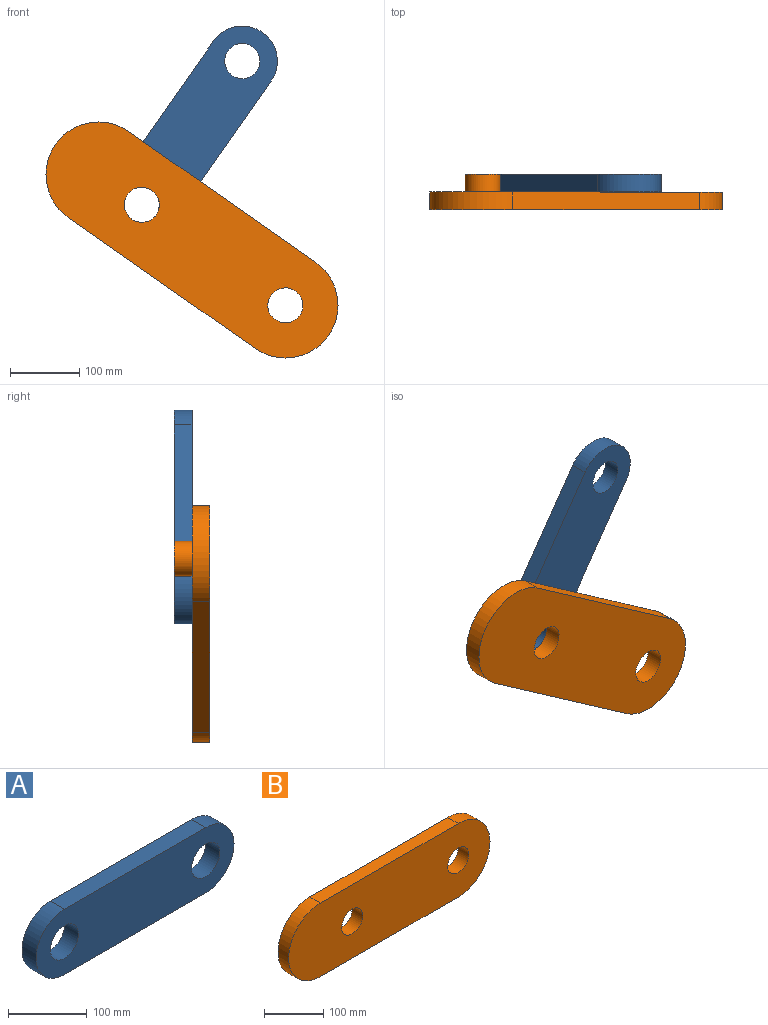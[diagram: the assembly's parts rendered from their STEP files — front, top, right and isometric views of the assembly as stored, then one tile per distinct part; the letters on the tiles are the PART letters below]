
ASSEMBLY  parts=2 mates=1
PART A: 8 faces, bbox 355.6x25.4x101.6 mm
  f0: plane 254x25.4mm, normal (0,0,1), area 6451.6mm2, adj f1,f4,f6,f7
  f1: cylinder r=50.8mm len=101.6mm, axis (0,1,0), area 4053.7mm2, adj f0,f2,f6,f7
  f2: plane 254x25.4mm, normal (0,0,-1), area 6451.6mm2, adj f1,f4,f6,f7
  f3: cylinder r=25.4mm len=50.8mm, axis (0,1,0), area 4053.7mm2, adj f6,f7
  f4: cylinder r=50.8mm len=101.6mm, axis (0,1,0), area 4053.7mm2, adj f0,f2,f6,f7
  f5: cylinder r=25.4mm len=50.8mm, axis (0,1,0), area 4053.7mm2, adj f6,f7
  f6: plane 355.6x101.6mm, normal (0,-1,0), area 29860.1mm2, adj f0,f1,f2,f3,f4,f5
  f7: plane 355.6x101.6mm, normal (0,1,0), area 29860.1mm2, adj f0,f1,f2,f3,f4,f5
PART B: 10 faces, bbox 482.6x50.8x152.4 mm
  f0: plane 330.2x25.4mm, normal (0,0,-1), area 8387.1mm2, adj f1,f5,f6,f7
  f1: cylinder r=76.2mm len=152.4mm, axis (0,1,0), area 6080.5mm2, adj f0,f2,f6,f7
  f2: plane 330.2x25.4mm, normal (0,0,1), area 8387.1mm2, adj f1,f5,f6,f7
  f3: cylinder r=25.4mm len=50.8mm, axis (0,1,0), area 4053.7mm2, adj f6,f7
  f4: cylinder r=25.4mm len=50.8mm, axis (0,1,0), area 4053.7mm2, adj f6,f7
  f5: cylinder r=76.2mm len=152.4mm, axis (0,1,0), area 6080.5mm2, adj f0,f2,f6,f7
  f6: plane 482.6x152.4mm, normal (0,-1,0), area 64510.3mm2, adj f0,f1,f2,f3,f4,f5
  f7: plane 482.6x152.4mm, normal (0,1,0), area 62483.5mm2, adj f0,f1,f2,f3,f4,f5,f8
  f8: cylinder r=25.4mm len=50.8mm, axis (0,-1,0), area 4053.7mm2, adj f7,f9
  f9: plane 50.8x50.8mm, normal (0,1,0), area 2026.8mm2, adj f8
PLACE A rot(axis=(0,-1,0),55deg) t=(-88.51,-57.83,-165.23)mm
PLACE B rot(axis=(0,1,0),35deg) t=(-88.51,-83.23,-165.23)mm
MATE revolute B.f3 <-> A.f1  axis (0,1,0) through (-88.51,-83.23,-165.23)mm
